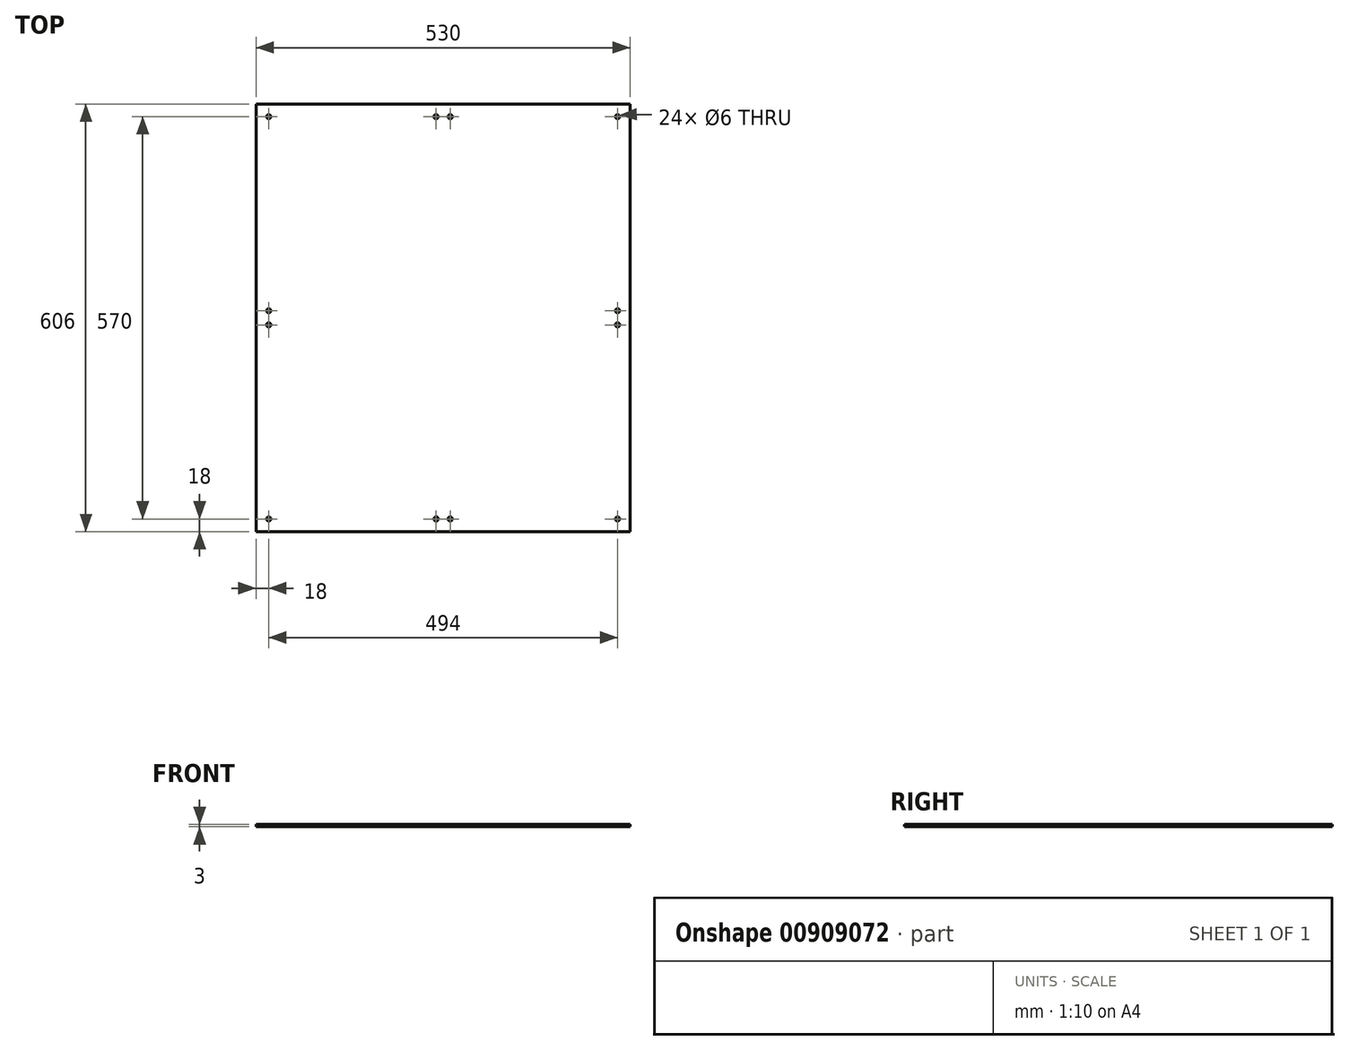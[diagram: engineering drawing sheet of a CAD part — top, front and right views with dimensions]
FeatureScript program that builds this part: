
annotation { "Feature Type Name" : "Feature", "Feature Type Description" : "" }
export const myFeature = defineFeature(function(context is Context, id is Id, definition is map)
    precondition{}
    {
        {
            var Q0;
            Q0=qCreatedBy(makeId("Top.planeOp"),FACE);
            var sketch = newSketch(context, id + "F0", { "sketchPlane" : qUnion([Q0])});
            skLineSegment(sketch, "E0.bottom", {"start": v(0, 0) * mm, "end": v(-530, 0) * mm});
            skLineSegment(sketch, "E0.top", {"start": v(0, 606) * mm, "end": v(-530, 606) * mm});
            skLineSegment(sketch, "E0.left", {"start": v(0, 0) * mm, "end": v(0, 606) * mm});
            skLineSegment(sketch, "E0.right", {"start": v(-530, 0) * mm, "end": v(-530, 606) * mm});
            skCircle(sketch, "E1", {"center": v(-512, 18) * mm, "radius": 3 * mm});
            skCircle(sketch, "E2", {"center": v(-18, 18) * mm, "radius": 3 * mm});
            skCircle(sketch, "E3", {"center": v(-512, 588) * mm, "radius": 3 * mm});
            skCircle(sketch, "E4", {"center": v(-18, 588) * mm, "radius": 3 * mm});
            skCircle(sketch, "E5", {"center": v(-275, 18) * mm, "radius": 3 * mm});
            skCircle(sketch, "E6", {"center": v(-255, 18) * mm, "radius": 3 * mm});
            skCircle(sketch, "E7", {"center": v(-512, 293) * mm, "radius": 3 * mm});
            skCircle(sketch, "E8", {"center": v(-512, 313) * mm, "radius": 3 * mm});
            skCircle(sketch, "E9", {"center": v(-18, 313) * mm, "radius": 3 * mm});
            skCircle(sketch, "E10", {"center": v(-18, 293) * mm, "radius": 3 * mm});
            skCircle(sketch, "E11", {"center": v(-275, 588) * mm, "radius": 3 * mm});
            skCircle(sketch, "E12", {"center": v(-255, 588) * mm, "radius": 3 * mm});
            skSolve(sketch);
        }
        {
            var Q0;
            Q0=makeQuery(id+"F0.imprint","IMPRINT",FACE,{"disambiguationData":[TD([[makeQuery(id+"F0.imprint","IMPRINT",EDGE,{"derivedFrom":sQuery(id+"F0.wireOp",EDGE,"E0.bottom")}),-1.0]])]});
            extrude(context, id + "F1", {"entities" : qUnion([Q0]), "depth" : 3 * mm, "offsetDistance" : 25 * mm});
        }
    });
